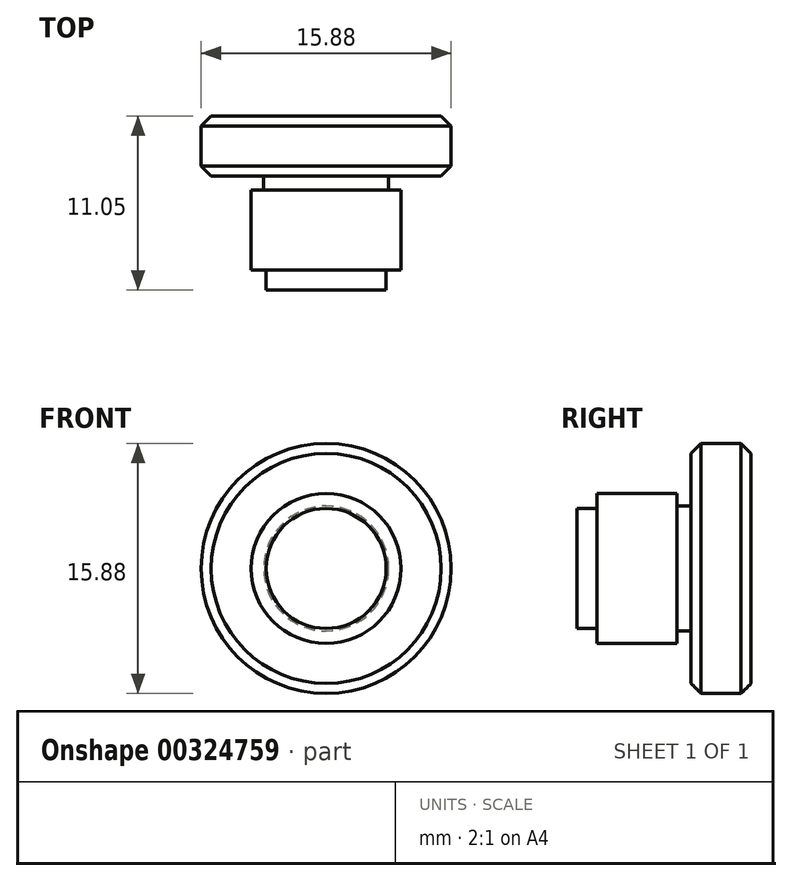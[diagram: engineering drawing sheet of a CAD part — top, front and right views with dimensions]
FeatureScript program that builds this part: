
annotation { "Feature Type Name" : "Feature", "Feature Type Description" : "" }
export const myFeature = defineFeature(function(context is Context, id is Id, definition is map)
    precondition{}
    {
        {
            var Q0;
            Q0=qCreatedBy(makeId("Front.planeOp"),FACE);
            var sketch = newSketch(context, id + "F0", { "sketchPlane" : qUnion([Q0])});
            skCircle(sketch, "E0", {"center": v(0, 0) * mm, "radius": 7.94 * mm});
            skSolve(sketch);
        }
        {
            var Q0;
            Q0=makeQuery(id+"F0.imprint","IMPRINT",FACE,{"disambiguationData":[TD([[makeQuery(id+"F0.imprint","IMPRINT",EDGE,{"derivedFrom":sQuery(id+"F0.wireOp",EDGE,"E0")}),1.0]])]});
            extrude(context, id + "F1", {"entities" : qUnion([Q0]), "depth" : 3.8 * mm, "offsetDistance" : 25.4 * mm});
        }
        {
            var Q0;
            Q0=makeQuery(id+"F1.opExtrude","CAP_FACE",FACE,{"disambiguationData":[OSD([sQuery(id+"F0.wireOp",EDGE,"E0")])],"isStart":false});
            var sketch = newSketch(context, id + "F2", { "sketchPlane" : qUnion([Q0])});
            skCircle(sketch, "E1", {"center": v(0, 0) * mm, "radius": 4.76 * mm});
            skSolve(sketch);
        }
        {
            var Q0;
            Q0=makeQuery(id+"F2.imprint","IMPRINT",FACE,{"disambiguationData":[TD([[makeQuery(id+"F2.imprint","IMPRINT",EDGE,{"derivedFrom":sQuery(id+"F2.wireOp",EDGE,"E1")}),1.0]])]});
            extrude(context, id + "F3", {"entities" : qUnion([Q0]), "depth" : 6.35 * mm, "offsetDistance" : 25.4 * mm});
        }
        {
            var Q0;
            Q0=makeQuery(id+"F3.opExtrude","SWEPT_BODY",BODY,{"disambiguationData":[OSD([sQuery(id+"F2.wireOp",EDGE,"E1")])]});
            deleteBodies(context, id + "F4", {"entities" : qUnion([Q0])});
        }
        {
            var Q0;
            Q0=makeQuery(id+"F1.opExtrude","CAP_FACE",FACE,{"disambiguationData":[OSD([sQuery(id+"F0.wireOp",EDGE,"E0")])],"isStart":false});
            var sketch = newSketch(context, id + "F5", { "sketchPlane" : qUnion([Q0])});
            skCircle(sketch, "E2", {"center": v(0, 0) * mm, "radius": 3.97 * mm});
            skSolve(sketch);
        }
        {
            var Q0;
            Q0=makeQuery(id+"F5.imprint","IMPRINT",FACE,{"disambiguationData":[TD([[makeQuery(id+"F5.imprint","IMPRINT",EDGE,{"derivedFrom":sQuery(id+"F5.wireOp",EDGE,"E2")}),1.0]])]});
            extrude(context, id + "F6", {"entities" : qUnion([Q0]), "operationType" : NewBodyOperationType.ADD, "depth" : 0.89 * mm, "offsetDistance" : 25.4 * mm});
        }
        {
            var Q0;
            Q0=makeQuery(id+"F6.opExtrude","CAP_FACE",FACE,{"disambiguationData":[OSD([sQuery(id+"F5.wireOp",EDGE,"E2")])],"isStart":false});
            var sketch = newSketch(context, id + "F7", { "sketchPlane" : qUnion([Q0])});
            skCircle(sketch, "E3", {"center": v(0, 0) * mm, "radius": 4.76 * mm});
            skSolve(sketch);
        }
        {
            var Q0;
            Q0=makeQuery(id+"F7.imprint","IMPRINT",FACE,{"disambiguationData":[TD([[makeQuery(id+"F7.imprint","IMPRINT",EDGE,{"derivedFrom":makeQuery(id+"F6.opExtrude","CAP_EDGE",EDGE,{"disambiguationData":[OSD([sQuery(id+"F5.wireOp",EDGE,"E2")])],"isStart":false})}),1.0]])]});
            var Q1;
            Q1=makeQuery(id+"F7.imprint","IMPRINT",FACE,{"disambiguationData":[TD([[makeQuery(id+"F7.imprint","IMPRINT",EDGE,{"derivedFrom":sQuery(id+"F7.wireOp",EDGE,"E3")}),1.0]])]});
            extrude(context, id + "F8", {"entities" : qUnion([Q0, Q1]), "operationType" : NewBodyOperationType.ADD, "depth" : 6.35 * mm, "offsetDistance" : 25.4 * mm});
        }
        {
            var Q0;
            Q0=makeQuery(id+"F8.opExtrude","CAP_FACE",FACE,{"disambiguationData":[OSD([sQuery(id+"F7.wireOp",EDGE,"E3")])],"isStart":false});
            var sketch = newSketch(context, id + "F9", { "sketchPlane" : qUnion([Q0])});
            skCircle(sketch, "E4", {"center": v(0, 0) * mm, "radius": 3.81 * mm});
            skSolve(sketch);
        }
        {
            var Q0;
            Q0=makeQuery(id+"F9.imprint","IMPRINT",FACE,{"disambiguationData":[TD([[makeQuery(id+"F9.imprint","IMPRINT",EDGE,{"derivedFrom":sQuery(id+"F9.wireOp",EDGE,"E4")}),-1.0]])]});
            extrude(context, id + "F10", {"entities" : qUnion([Q0]), "operationType" : NewBodyOperationType.REMOVE, "oppositeDirection" : true, "depth" : 1.27 * mm, "offsetDistance" : 25.4 * mm});
        }
        {
            var Q0;
            Q0=makeQuery(id+"F1.opExtrude","CAP_EDGE",EDGE,{"disambiguationData":[OSD([sQuery(id+"F0.wireOp",EDGE,"E0")])],"isStart":false});
            var Q1;
            Q1=makeQuery(id+"F1.opExtrude","CAP_EDGE",EDGE,{"disambiguationData":[OSD([sQuery(id+"F0.wireOp",EDGE,"E0")])],"isStart":true});
            chamfer(context, id + "F11", {"entities" : qUnion([Q0, Q1]), "width" : 0.64 * mm, "tangentPropagation" : true});
        }
    });
